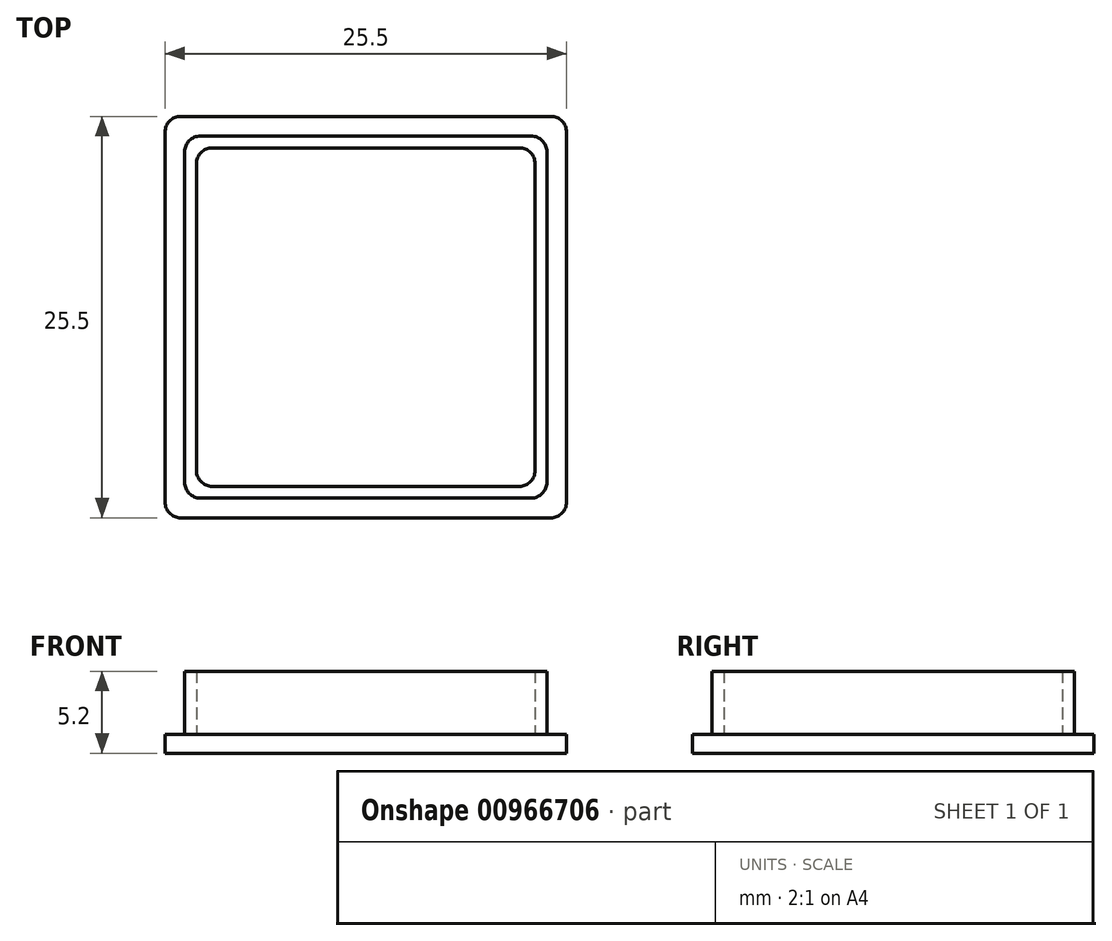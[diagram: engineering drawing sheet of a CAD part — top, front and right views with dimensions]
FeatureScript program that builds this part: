
annotation { "Feature Type Name" : "Feature", "Feature Type Description" : "" }
export const myFeature = defineFeature(function(context is Context, id is Id, definition is map)
    precondition{}
    {
        {
            var Q0;
            Q0=qCreatedBy(makeId("Top.planeOp"),FACE);
            var sketch = newSketch(context, id + "F0", { "sketchPlane" : qUnion([Q0])});
            skLineSegment(sketch, "E0.bottom", {"start": v(12.75, -12.75) * mm, "end": v(-12.75, -12.75) * mm});
            skLineSegment(sketch, "E0.top", {"start": v(12.75, 12.75) * mm, "end": v(-12.75, 12.75) * mm});
            skLineSegment(sketch, "E0.left", {"start": v(12.75, -12.75) * mm, "end": v(12.75, 12.75) * mm});
            skLineSegment(sketch, "E0.right", {"start": v(-12.75, -12.75) * mm, "end": v(-12.75, 12.75) * mm});
            skPoint(sketch, "E0.middle", {"position": v(0, 0) * mm});
            skSolve(sketch);
        }
        {
            var Q0;
            Q0=makeQuery(id+"F0.imprint","IMPRINT",FACE,{"disambiguationData":[TD([[makeQuery(id+"F0.imprint","IMPRINT",EDGE,{"derivedFrom":sQuery(id+"F0.wireOp",EDGE,"E0.bottom")}),-1.0]])]});
            extrude(context, id + "F1", {"entities" : qUnion([Q0]), "depth" : 1.2 * mm, "offsetDistance" : 25 * mm});
        }
        {
            var Q0;
            Q0=makeQuery(id+"F1.opExtrude","CAP_FACE",FACE,{"disambiguationData":[OSD([sQuery(id+"F0.wireOp",EDGE,"E0.bottom"),sQuery(id+"F0.wireOp",EDGE,"E0.top"),sQuery(id+"F0.wireOp",EDGE,"E0.left"),sQuery(id+"F0.wireOp",EDGE,"E0.right")])],"isStart":false});
            var sketch = newSketch(context, id + "F2", { "sketchPlane" : qUnion([Q0])});
            skLineSegment(sketch, "E1.bottom", {"start": v(11.5, -11.5) * mm, "end": v(-11.5, -11.5) * mm});
            skLineSegment(sketch, "E1.top", {"start": v(11.5, 11.5) * mm, "end": v(-11.5, 11.5) * mm});
            skLineSegment(sketch, "E1.left", {"start": v(11.5, -11.5) * mm, "end": v(11.5, 11.5) * mm});
            skLineSegment(sketch, "E1.right", {"start": v(-11.5, -11.5) * mm, "end": v(-11.5, 11.5) * mm});
            skPoint(sketch, "E1.middle", {"position": v(0, 0) * mm});
            skLineSegment(sketch, "E2.bottom", {"start": v(10.75, -10.75) * mm, "end": v(-10.75, -10.75) * mm});
            skLineSegment(sketch, "E2.top", {"start": v(10.75, 10.75) * mm, "end": v(-10.75, 10.75) * mm});
            skLineSegment(sketch, "E2.left", {"start": v(10.75, -10.75) * mm, "end": v(10.75, 10.75) * mm});
            skLineSegment(sketch, "E2.right", {"start": v(-10.75, -10.75) * mm, "end": v(-10.75, 10.75) * mm});
            skSolve(sketch);
        }
        {
            var Q0;
            Q0=makeQuery(id+"F2.imprint","IMPRINT",FACE,{"disambiguationData":[TD([[makeQuery(id+"F2.imprint","IMPRINT",EDGE,{"derivedFrom":sQuery(id+"F2.wireOp",EDGE,"E1.bottom")}),-1.0]])]});
            extrude(context, id + "F3", {"entities" : qUnion([Q0]), "operationType" : NewBodyOperationType.ADD, "depth" : 4 * mm, "offsetDistance" : 25 * mm});
        }
        {
            var Q0;
            Q0=makeQuery(id+"F3.opExtrude","SWEPT_EDGE",EDGE,{"disambiguationData":[OSD([sQuery(id+"F2.wireOp",EDGE,"E2.top"),sQuery(id+"F2.wireOp",EDGE,"E2.right")])]});
            var Q1;
            Q1=makeQuery(id+"F3.opExtrude","SWEPT_EDGE",EDGE,{"disambiguationData":[OSD([sQuery(id+"F2.wireOp",EDGE,"E2.top"),sQuery(id+"F2.wireOp",EDGE,"E2.left")])]});
            var Q2;
            Q2=makeQuery(id+"F3.opExtrude","SWEPT_EDGE",EDGE,{"disambiguationData":[OSD([sQuery(id+"F2.wireOp",EDGE,"E2.bottom"),sQuery(id+"F2.wireOp",EDGE,"E2.left")])]});
            var Q3;
            Q3=makeQuery(id+"F3.opExtrude","SWEPT_EDGE",EDGE,{"disambiguationData":[OSD([sQuery(id+"F2.wireOp",EDGE,"E2.bottom"),sQuery(id+"F2.wireOp",EDGE,"E2.right")])]});
            fillet(context, id + "F4", {"entities" : qUnion([Q0, Q1, Q2, Q3]), "radius" : 1 * mm, "tangentPropagation" : true, "allowEdgeOverflow" : false});
        }
        {
            var Q0;
            Q0=makeQuery(id+"F3.opExtrude","SWEPT_EDGE",EDGE,{"disambiguationData":[OSD([sQuery(id+"F2.wireOp",EDGE,"E1.top"),sQuery(id+"F2.wireOp",EDGE,"E1.left")])]});
            var Q1;
            Q1=makeQuery(id+"F3.opExtrude","SWEPT_EDGE",EDGE,{"disambiguationData":[OSD([sQuery(id+"F2.wireOp",EDGE,"E1.bottom"),sQuery(id+"F2.wireOp",EDGE,"E1.left")])]});
            var Q2;
            Q2=makeQuery(id+"F3.opExtrude","SWEPT_EDGE",EDGE,{"disambiguationData":[OSD([sQuery(id+"F2.wireOp",EDGE,"E1.top"),sQuery(id+"F2.wireOp",EDGE,"E1.right")])]});
            var Q3;
            Q3=makeQuery(id+"F3.opExtrude","SWEPT_EDGE",EDGE,{"disambiguationData":[OSD([sQuery(id+"F2.wireOp",EDGE,"E1.bottom"),sQuery(id+"F2.wireOp",EDGE,"E1.right")])]});
            var Q4;
            Q4=makeQuery(id+"F1.opExtrude","SWEPT_EDGE",EDGE,{"disambiguationData":[OSD([sQuery(id+"F0.wireOp",EDGE,"E0.top"),sQuery(id+"F0.wireOp",EDGE,"E0.right")])]});
            var Q5;
            Q5=makeQuery(id+"F1.opExtrude","SWEPT_EDGE",EDGE,{"disambiguationData":[OSD([sQuery(id+"F0.wireOp",EDGE,"E0.top"),sQuery(id+"F0.wireOp",EDGE,"E0.left")])]});
            var Q6;
            Q6=makeQuery(id+"F1.opExtrude","SWEPT_EDGE",EDGE,{"disambiguationData":[OSD([sQuery(id+"F0.wireOp",EDGE,"E0.bottom"),sQuery(id+"F0.wireOp",EDGE,"E0.left")])]});
            var Q7;
            Q7=makeQuery(id+"F1.opExtrude","SWEPT_EDGE",EDGE,{"disambiguationData":[OSD([sQuery(id+"F0.wireOp",EDGE,"E0.bottom"),sQuery(id+"F0.wireOp",EDGE,"E0.right")])]});
            fillet(context, id + "F5", {"entities" : qUnion([Q0, Q1, Q2, Q3, Q4, Q5, Q6, Q7]), "radius" : 1 * mm, "tangentPropagation" : true, "allowEdgeOverflow" : false});
        }
    });
